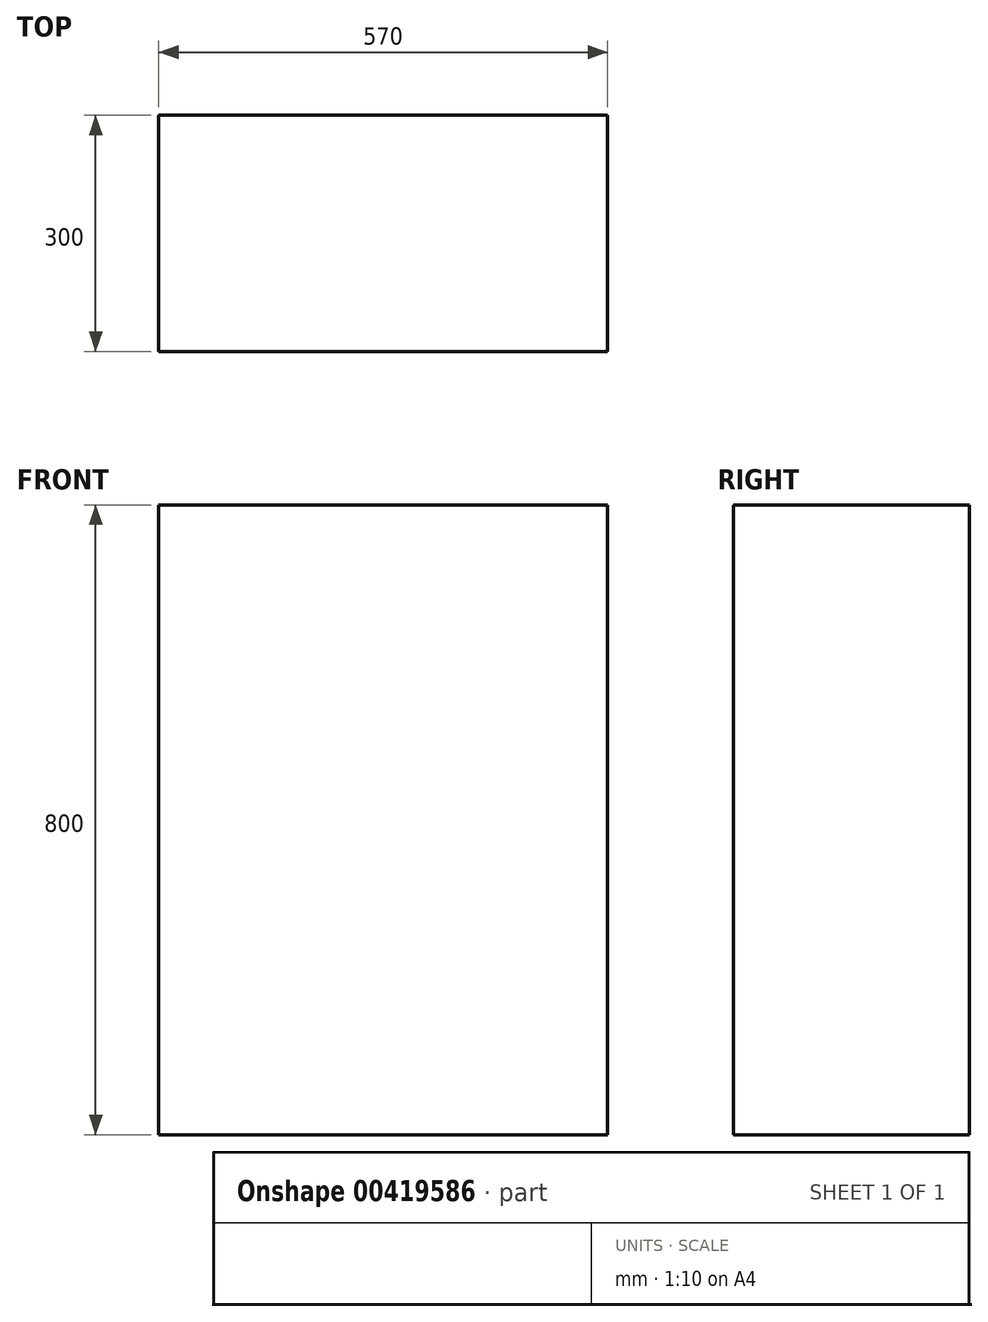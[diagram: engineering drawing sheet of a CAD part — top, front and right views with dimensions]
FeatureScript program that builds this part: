
annotation { "Feature Type Name" : "Feature", "Feature Type Description" : "" }
export const myFeature = defineFeature(function(context is Context, id is Id, definition is map)
    precondition{}
    {
        {
            var Q0;
            Q0=qCreatedBy(makeId("Top.planeOp"),FACE);
            var sketch = newSketch(context, id + "F0", { "sketchPlane" : qUnion([Q0])});
            skLineSegment(sketch, "E0.bottom", {"start": v(-495.14, 255.99) * mm, "end": v(74.86, 255.99) * mm});
            skLineSegment(sketch, "E0.top", {"start": v(-495.14, -44.01) * mm, "end": v(74.86, -44.01) * mm});
            skLineSegment(sketch, "E0.left", {"start": v(-495.14, 255.99) * mm, "end": v(-495.14, -44.01) * mm});
            skLineSegment(sketch, "E0.right", {"start": v(74.86, 255.99) * mm, "end": v(74.86, -44.01) * mm});
            skSolve(sketch);
        }
        {
            var Q0;
            Q0=makeQuery(id+"F0.imprint","IMPRINT",FACE,{"disambiguationData":[TD([[makeQuery(id+"F0.imprint","IMPRINT",EDGE,{"derivedFrom":sQuery(id+"F0.wireOp",EDGE,"E0.bottom")}),-1.0]])]});
            extrude(context, id + "F1", {"entities" : qUnion([Q0]), "depth" : 800 * mm});
        }
    });
